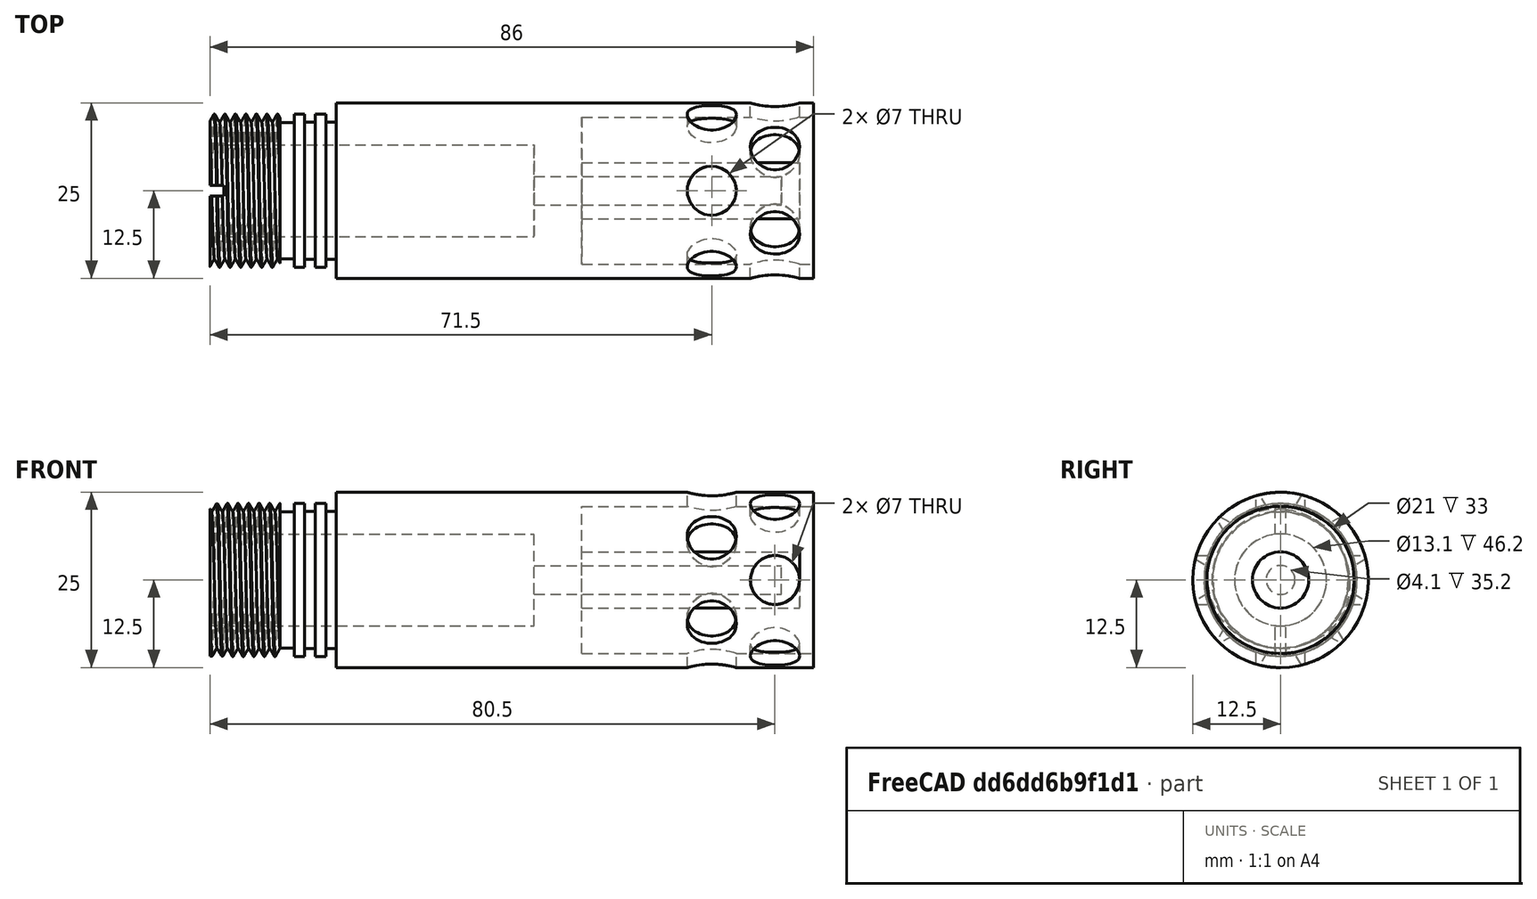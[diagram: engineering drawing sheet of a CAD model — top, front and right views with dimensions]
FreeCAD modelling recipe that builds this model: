
FCSTD DOCUMENT  (FreeCAD 0.17R13541 (Git))
Label: ERG-T-04-HEAD-01
License: All rights reserved
LicenseURL: http://en.wikipedia.org/wiki/All_rights_reserved
objects: Drawing::FeatureViewPython×37, Part::Cylinder×25, Part::Cut×13, Part::MultiFuse×9, Drawing::FeatureViewPart×4, Part::Helix×1, Sketcher::SketchObject×1, Part::Sweep×1, Part::Box×1, Drawing::FeaturePage×1
note: 51 computed .brp shape members not serialized (recipe doc carries the construction recipe); baked Part::Feature solids carry a one-line shape summary decoded from their .brp

FEATURE [Part::Cylinder] Cylinder072  label="Cylinder077"
  Angle = 360
  AttacherType = Attacher::AttachEngine3D
  Height = 18
  Placement = pos=(180.5,0,0) rot=(0,1,0;1.5708rad)
  Radius = 10.9
FEATURE [Part::Cylinder] Cylinder074  label="Cylinder083"
  Angle = 360
  AttacherType = Attacher::AttachEngine3D
  Height = 46.2
  Placement = pos=(180.5,0,0) rot=(0,1,0;1.5708rad)
  Radius = 6.55
FEATURE [Part::Cylinder] Cylinder075  label="Cylinder084"
  Angle = 360
  AttacherType = Attacher::AttachEngine3D
  Height = 53
  Placement = pos=(180.5,0,0) rot=(0,1,0;1.5708rad)
  Radius = 12.5
FEATURE [Part::Cylinder] Cylinder076  label="Cylinder085"
  Angle = 360
  AttacherType = Attacher::AttachEngine3D
  Height = 18
  Placement = pos=(180.5,0,0) rot=(0,1,0;1.5708rad)
  Radius = 12.5
FEATURE [Part::Cylinder] Cylinder077  label="Cylinder086"
  Angle = 360
  AttacherType = Attacher::AttachEngine3D
  Height = 31
  Placement = pos=(233.5,0,0) rot=(0,1,0;1.5708rad)
  Radius = 4
FEATURE [Part::Cut] Cut065
  Base = -> Cylinder076
  Tool = -> Cylinder072
FEATURE [Part::Cylinder] Cylinder080  label="Cylinder089"
  Angle = 360
  AttacherType = Attacher::AttachEngine3D
  Height = 35.2
  Placement = pos=(226.7,0,0) rot=(0,1,0;1.5708rad)
  Radius = 2.05
FEATURE [Part::MultiFuse] Fusion017  label="cavity"
  Shapes = -> [Cylinder080,Cylinder074]
FEATURE [Part::Helix] Helix019
  Angle = 0
  AttacherType = Attacher::AttachEngine3D
  Height = 17
  LocalCoord = 0
  Pitch = 1.5
  Placement = pos=(157,0,0) rot=(0,1,0;1.5708rad)
  Radius = 10.5
  Style = 1
FEATURE [Sketcher::SketchObject] Sketch023  label="T022"
  Placement = pos=(157,0,-11.01) rot=(1,0,0;1.5708rad)
  sketch-geometry (3):
    g0: LineSegment StartX=0 StartY=1.29904 StartZ=0 EndX=-0.75 EndY=0 EndZ=0
    g1: LineSegment StartX=0.75 StartY=0 StartZ=0 EndX=0 EndY=1.29904 EndZ=0
    g2: LineSegment StartX=-0.75 StartY=0 StartZ=0 EndX=0.75 EndY=0 EndZ=0
  constraints (9):
    c: PointOnObject(g1,g-1)
    c: Coincident(g1,g0)
    c: Coincident(g2,g0)
    c: Coincident(g2,g1)
    c: Horizontal(g2)
    c: Symmetric(g0,g1,g-2)
    c: Distance(g0,g1) = 1.5
    c: Angle(g1,g2) = 1.0472
    c: Angle(g2,g0) = 1.0472
FEATURE [Part::Sweep] Sweep016
  Frenet = true
  Sections = -> [Sketch023]
  Solid = true
  Spine = -> Helix019
  Transition = 1
FEATURE [Part::Cylinder] Cylinder084  label="Cylinder092"
  Angle = 360
  AttacherType = Attacher::AttachEngine3D
  Height = 1.5
  Placement = pos=(178,0,0) rot=(0,1,0;1.5708rad)
  Radius = 11
FEATURE [Part::Cylinder] Cylinder085  label="Cylinder093"
  Angle = 360
  AttacherType = Attacher::AttachEngine3D
  Height = 1.5
  Placement = pos=(178,0,0) rot=(0,1,0;1.5708rad)
  Radius = 9.8
FEATURE [Part::Cut] Cut071  label="circ2"
  Base = -> Cylinder084
  Placement = pos=(16,0,0) rot=(0,0,1;0rad)
  Tool = -> Cylinder085
FEATURE [Part::Cylinder] Cylinder086  label="Cylinder094"
  Angle = 360
  AttacherType = Attacher::AttachEngine3D
  Height = 2
  Placement = pos=(178,0,0) rot=(0,1,0;1.5708rad)
  Radius = 11
FEATURE [Part::Cylinder] Cylinder087  label="Cylinder095"
  Angle = 360
  AttacherType = Attacher::AttachEngine3D
  Height = 2
  Placement = pos=(178,0,0) rot=(0,1,0;1.5708rad)
  Radius = 9.7
FEATURE [Part::Cut] Cut072  label="circ1"
  Base = -> Cylinder086
  Placement = pos=(12.5,0,0) rot=(0,0,1;0rad)
  Tool = -> Cylinder087
FEATURE [Part::Cylinder] Cylinder088  label="Cylinder096"
  Angle = 360
  AttacherType = Attacher::AttachEngine3D
  Height = 10
  Placement = pos=(178,0,0) rot=(0,1,0;1.5708rad)
  Radius = 9
FEATURE [Part::Cylinder] Cylinder089  label="Cylinder097"
  Angle = 360
  AttacherType = Attacher::AttachEngine3D
  Height = 10
  Placement = pos=(178,0,0) rot=(0,1,0;1.5708rad)
  Radius = 11.5
FEATURE [Part::Cut] Cut074
  Base = -> Cylinder089
  Placement = pos=(-10.5,0,0) rot=(0,0,1;0rad)
  Tool = -> Cylinder088
FEATURE [Part::Box] Box  label="Cube"
  AttacherType = Attacher::AttachEngine3D
  Height = 30
  Length = 2
  Placement = pos=(180.5,-0.75,-15) rot=(0,0,1;0rad)
  Width = 1.5
FEATURE [Part::Cylinder] Cylinder091  label="Cylinder099"
  Angle = 360
  AttacherType = Attacher::AttachEngine3D
  Height = 35
  Placement = pos=(198.5,0,0) rot=(0,1,0;1.5708rad)
  Radius = 12.5
FEATURE [Part::Cylinder] Cylinder092  label="Cylinder100"
  Angle = 360
  AttacherType = Attacher::AttachEngine3D
  Height = 35
  Placement = pos=(198.5,0,0) rot=(0,1,0;1.5708rad)
  Radius = 10.9
FEATURE [Part::Cut] Cut
  Base = -> Cylinder091
  Tool = -> Cylinder092
FEATURE [Part::Cylinder] Cylinder093  label="Cylinder101"
  Angle = 360
  AttacherType = Attacher::AttachEngine3D
  Height = 1.5
  Placement = pos=(178,0,0) rot=(0,1,0;1.5708rad)
  Radius = 11
FEATURE [Part::Cylinder] Cylinder094  label="Cylinder102"
  Angle = 360
  AttacherType = Attacher::AttachEngine3D
  Height = 1.5
  Placement = pos=(178,0,0) rot=(0,1,0;1.5708rad)
  Radius = 9.8
FEATURE [Part::Cut] Cut076  label="circ3"
  Base = -> Cylinder093
  Placement = pos=(19,0,0) rot=(0,0,1;0rad)
  Tool = -> Cylinder094
FEATURE [Part::MultiFuse] Fusion019
  Shapes = -> [Cut,Cut065]
FEATURE [Part::MultiFuse] Fusion020
  Shapes = -> [Cylinder075,Cylinder077]
FEATURE [Part::Cut] Cut077  label="body"
  Base = -> Fusion020
  Tool = -> Fusion019
FEATURE [Part::Cut] Cut078  label="thread"
  Base = -> Sweep016
  Placement = pos=(23,0,0) rot=(0,0,1;0rad)
  Tool = -> Cut074
FEATURE [Part::MultiFuse] Fusion021  label="cutstuff"
  Shapes = -> [Cut078,Cut076,Cut072,Cut071]
FEATURE [Part::Cut] Cut079  label="outside"
  Base = -> Cut077
  Tool = -> Fusion021
FEATURE [Part::Cut] Cut080  label="holder01"
  Base = -> Cut079
  Tool = -> Fusion017
FEATURE [Part::Cut] Cut081  label="HOLDER"
  Base = -> Cut080
  Tool = -> Box
FEATURE [Part::Cylinder] Cylinder079  label="Cylinder088"
  Angle = 360
  AttacherType = Attacher::AttachEngine3D
  Height = 50
  Placement = pos=(214.2,21.6506,12.5) rot=(1,0,0;2.0944rad)
  Radius = 3.5
FEATURE [Part::Cylinder] Cylinder081  label="Cylinder090"
  Angle = 360
  AttacherType = Attacher::AttachEngine3D
  Height = 50
  Placement = pos=(214.2,0,-25) rot=(0,1,0;0rad)
  Radius = 3.5
FEATURE [Part::Cylinder] Cylinder082  label="Cylinder078"
  Angle = 360
  AttacherType = Attacher::AttachEngine3D
  Height = 50
  Placement = pos=(214.2,0,-25) rot=(0,1,0;0rad)
  Radius = 3.5
FEATURE [Part::Cylinder] Cylinder090  label="Cylinder098"
  Angle = 360
  AttacherType = Attacher::AttachEngine3D
  Height = 68
  Placement = pos=(198.2,0,0) rot=(0,1,0;1.5708rad)
  Radius = 12.5
FEATURE [Part::Cylinder] Cylinder071  label="Cylinder081"
  Angle = 360
  AttacherType = Attacher::AttachEngine3D
  Height = 33
  Placement = pos=(233.2,0,0) rot=(0,1,0;1.5708rad)
  Radius = 10.5
FEATURE [Part::Cylinder] Cylinder095  label="Cylinder103"
  Angle = 360
  AttacherType = Attacher::AttachEngine3D
  Height = 35
  Placement = pos=(198.2,0,0) rot=(0,1,0;1.5708rad)
  Radius = 10.9
FEATURE [Part::MultiFuse] Fusion022  label="cavity001"
  Shapes = -> [Cylinder095,Cylinder071]
FEATURE [Part::Cut] Cut082  label="body001"
  Base = -> Cylinder090
  Tool = -> Fusion022
FEATURE [Part::Cylinder] Cylinder070  label="Cylinder075"
  Angle = 360
  AttacherType = Attacher::AttachEngine3D
  Height = 50
  Placement = pos=(214.2,-21.6506,12.5) rot=(-1,0,0;2.0944rad)
  Radius = 3.5
FEATURE [Part::Cylinder] Cylinder078  label="Cylinder087"
  Angle = 360
  AttacherType = Attacher::AttachEngine3D
  Height = 50
  Placement = pos=(214.2,21.6506,12.5) rot=(1,0,0;2.0944rad)
  Radius = 3.5
FEATURE [Part::MultiFuse] Fusion016
  Placement = pos=(37.5,0,0) rot=(1,0,0;0rad)
  Shapes = -> [Cylinder081,Cylinder070,Cylinder078]
FEATURE [Part::Cylinder] Cylinder073  label="Cylinder082"
  Angle = 360
  AttacherType = Attacher::AttachEngine3D
  Height = 50
  Placement = pos=(214.2,-21.6506,12.5) rot=(-1,0,0;2.0944rad)
  Radius = 3.5
FEATURE [Part::MultiFuse] Fusion018
  Placement = pos=(46.5,0,0) rot=(1,0,0;0.523599rad)
  Shapes = -> [Cylinder082,Cylinder073,Cylinder079]
FEATURE [Part::MultiFuse] Fusion  label="holesticks"
  Shapes = -> [Fusion016,Fusion018]
FEATURE [Part::Cut] Cut001  label="CAP"
  Base = -> Cut082
  Placement = pos=(0.3,0,0) rot=(0,0,1;0rad)
  Tool = -> Fusion
FEATURE [Part::MultiFuse] Fusion023  label="SensorHead"
  Shapes = -> [Cut081,Cut001]
FEATURE [Drawing::FeatureViewPart] Ortho  label="Ortho_0_0"
  Direction = (0,0,1)
  HiddenWidth = 0.15
  LineWidth = 0.35
  Rotation = 0
  Scale = 1.5
  ShowHiddenLines = true
  ShowSmoothLines = false
  Source = -> Fusion023
  Tolerance = 0.05
  ViewResult = <blob: 68235 chars omitted>
  Visible = true
  X = -186.75
  Y = 110.035
FEATURE [Drawing::FeatureViewPart] Ortho001  label="Ortho_0_1"
  Direction = (0,1,0)
  HiddenWidth = 0.15
  LineWidth = 0.35
  Rotation = 90
  Scale = 1.5
  ShowHiddenLines = true
  ShowSmoothLines = false
  Source = -> Fusion023
  Tolerance = 0.05
  ViewResult = <blob: 71833 chars omitted>
  Visible = true
  X = -186.75
  Y = 48.0517
FEATURE [Drawing::FeatureViewPart] Ortho002  label="Ortho_-1_0"
  Direction = (-1,0,0)
  HiddenWidth = 0.15
  LineWidth = 0.35
  Rotation = 180
  Scale = 1.5
  ShowHiddenLines = false
  ShowSmoothLines = false
  Source = -> Fusion023
  Tolerance = 0.05
  ViewResult = <blob: 14016 chars omitted>
  Visible = true
  X = 53.8386
  Y = 110.035
FEATURE [Drawing::FeatureViewPart] Ortho003  label="Ortho_1_0"
  Direction = (1,0,0)
  HiddenWidth = 0.15
  LineWidth = 0.35
  Rotation = 180
  Scale = 1.5
  ShowHiddenLines = false
  ShowSmoothLines = false
  Source = -> Fusion023
  Tolerance = 0.05
  ViewResult = <blob: 12692 chars omitted>
  Visible = true
  X = 243.161
  Y = 110.035
FEATURE [Drawing::FeatureViewPython] dia001  # drawing view (typed FeaturePython)
  Rotation = 0
  ViewResult = <g>  <circle cx ="243.161000" cy ="110.035000" r="0.250000" stroke="none" fill="rgb(255,0,0)" /> \n<line x1="265.734526" y1="88.241056" x2="238.844478" y2="114.202450" style="stroke:rgb(255,0,0);stroke-width:0.10" />\n<polygon points="247.477522,105.867550 245.691394,106.896990 245.678971,107.603988 246.385969,107.616410" style="fill:rgb(255,0,0);stroke:rgb(255,0,0);stroke-width:0" />\n<polygon points="238.844478,114.202450 240.630606,113.173010 240.643029,112.466012 239.936031,112.453590" style="fill:rgb(255,0,0);stroke:rgb(255,0,0);stroke-width:0" />\n<line x1="265.734526" y1="88.241056" x2="277.870832" y2="88.241056" style="stroke:rgb(255,0,0);stroke-width:0.10" />\n<text x="271.802679" y="86.241056" font-family="inherit" font-size="3.6" fill="rgb(0,0,0)" text-anchor="middle" transform="rotate(0.000000 271.802679,86.241056)" >Ø8</text> </g>
  Visible = true
  X = 0
  Y = 0
  arrowL1 = 2
  arrowL2 = 0.5
  arrowW = 1
  arrow_scheme = 0
  autoPlaceOffset = 2
  autoPlaceText = true
  centerPointDia = 0.5
  click1_x = 265.735
  click1_y = 88.2411
  click2_x = 277.871
  click2_y = 88.4939
  click3_x = 277.871
  click3_y = 88.4939
  comma_decimal_place = false
  lineColor = rgb(255,0,0)
  strokeWidth = 0.1
  textFormat_circular = Ø%(value)3.3f
  textRenderer_color = rgb(0,0,0)
  textRenderer_family = inherit
  textRenderer_size = 3.6
  unit_custom_scale = 1
  unit_scheme = 0
FEATURE [Drawing::FeatureViewPython] dia002  # drawing view (typed FeaturePython)
  Rotation = 0
  ViewResult = <g>  <circle cx ="243.161000" cy ="110.035000" r="0.250000" stroke="none" fill="rgb(255,0,0)" /> \n<line x1="263.711809" y1="131.476645" x2="232.262781" y2="98.664366" style="stroke:rgb(255,0,0);stroke-width:0.10" />\n<polygon points="254.059219,121.405634 253.036290,119.615769 252.329343,119.600772 252.314345,120.307720" style="fill:rgb(255,0,0);stroke:rgb(255,0,0);stroke-width:0" />\n<polygon points="232.262781,98.664366 233.285710,100.454231 233.992657,100.469228 234.007655,99.762280" style="fill:rgb(255,0,0);stroke:rgb(255,0,0);stroke-width:0" />\n<line x1="263.711809" y1="131.476645" x2="273.319717" y2="131.476645" style="stroke:rgb(255,0,0);stroke-width:0.10" />\n<text x="268.515763" y="129.476645" font-family="inherit" font-size="3.6" fill="rgb(0,0,0)" text-anchor="middle" transform="rotate(0.000000 268.515763,129.476645)" >Ø21</text> </g>
  Visible = true
  X = 0
  Y = 0
  arrowL1 = 2
  arrowL2 = 0.5
  arrowW = 1
  arrow_scheme = 0
  autoPlaceOffset = 2
  autoPlaceText = true
  centerPointDia = 0.5
  click1_x = 263.712
  click1_y = 131.477
  click2_x = 273.32
  click2_y = 132.994
  click3_x = 273.32
  click3_y = 132.994
  comma_decimal_place = false
  lineColor = rgb(255,0,0)
  strokeWidth = 0.1
  textFormat_circular = Ø%(value)3.3f
  textRenderer_color = rgb(0,0,0)
  textRenderer_family = inherit
  textRenderer_size = 3.6
  unit_custom_scale = 1
  unit_scheme = 0
FEATURE [Drawing::FeatureViewPython] dia003  # drawing view (typed FeaturePython)
  Rotation = 0
  ViewResult = <g>  <circle cx ="243.161000" cy ="110.035000" r="0.250000" stroke="none" fill="rgb(255,0,0)" /> \n<line x1="255.115259" y1="139.820355" x2="236.177225" y2="92.634155" style="stroke:rgb(255,0,0);stroke-width:0.10" />\n<polygon points="250.144775,127.435845 249.863861,125.393521 249.213605,125.115732 248.935816,125.765989" style="fill:rgb(255,0,0);stroke:rgb(255,0,0);stroke-width:0" />\n<polygon points="236.177225,92.634155 236.458139,94.676479 237.108395,94.954268 237.386184,94.304011" style="fill:rgb(255,0,0);stroke:rgb(255,0,0);stroke-width:0" />\n<line x1="255.115259" y1="139.820355" x2="263.458969" y2="139.820355" style="stroke:rgb(255,0,0);stroke-width:0.10" />\n<text x="259.287114" y="137.820355" font-family="inherit" font-size="3.6" fill="rgb(0,0,0)" text-anchor="middle" transform="rotate(0.000000 259.287114,137.820355)" >Ø25</text> </g>
  Visible = true
  X = 0
  Y = 0
  arrowL1 = 2
  arrowL2 = 0.5
  arrowW = 1
  arrow_scheme = 0
  autoPlaceOffset = 2
  autoPlaceText = true
  centerPointDia = 0.5
  click1_x = 255.115
  click1_y = 139.82
  click2_x = 263.459
  click2_y = 143.36
  click3_x = 263.459
  click3_y = 143.36
  comma_decimal_place = false
  lineColor = rgb(255,0,0)
  strokeWidth = 0.1
  textFormat_circular = Ø%(value)3.3f
  textRenderer_color = rgb(0,0,0)
  textRenderer_family = inherit
  textRenderer_size = 3.6
  unit_custom_scale = 1
  unit_scheme = 0
FEATURE [Drawing::FeatureViewPython] dia004  # drawing view (typed FeaturePython)
  Rotation = 0
  ViewResult = <g>  <circle cx ="53.838600" cy ="110.035008" r="0.250000" stroke="none" fill="rgb(255,0,0)" /> \n<line x1="21.744214" y1="149.681103" x2="60.020464" y2="102.398570" style="stroke:rgb(255,0,0);stroke-width:0.10" />\n<polygon points="47.656736,117.671446 49.303753,116.431553 49.229729,115.728332 48.526508,115.802356" style="fill:rgb(255,0,0);stroke:rgb(255,0,0);stroke-width:0" />\n<polygon points="60.020464,102.398570 58.373447,103.638463 58.447471,104.341684 59.150692,104.267660" style="fill:rgb(255,0,0);stroke:rgb(255,0,0);stroke-width:0" />\n<line x1="21.744214" y1="149.681103" x2="12.389145" y2="149.681103" style="stroke:rgb(255,0,0);stroke-width:0.10" />\n<text x="17.066680" y="147.681103" font-family="inherit" font-size="3.6" fill="rgb(0,0,0)" text-anchor="middle" transform="rotate(0.000000 17.066680,147.681103)" >Ø13.1</text> </g>
  Visible = true
  X = 0
  Y = 0
  arrowL1 = 2
  arrowL2 = 0.5
  arrowW = 1
  arrow_scheme = 0
  autoPlaceOffset = 2
  autoPlaceText = true
  centerPointDia = 0.5
  click1_x = 21.7442
  click1_y = 149.681
  click2_x = 12.3891
  click2_y = 148.67
  click3_x = 12.3891
  click3_y = 148.67
  comma_decimal_place = false
  lineColor = rgb(255,0,0)
  strokeWidth = 0.1
  textFormat_circular = Ø%(value)3.3f
  textRenderer_color = rgb(0,0,0)
  textRenderer_family = inherit
  textRenderer_size = 3.6
  unit_custom_scale = 1
  unit_scheme = 0
FEATURE [Drawing::FeatureViewPython] dia005  # drawing view (typed FeaturePython)
  Rotation = 0
  ViewResult = <g>  <circle cx ="53.838600" cy ="110.035000" r="0.250000" stroke="none" fill="rgb(255,0,0)" /> \n<line x1="31.099283" y1="81.667224" x2="55.761862" y2="112.434310" style="stroke:rgb(255,0,0);stroke-width:0.10" />\n<polygon points="51.915338,107.635690 52.776108,109.508942 53.478966,109.586349 53.556372,108.883491" style="fill:rgb(255,0,0);stroke:rgb(255,0,0);stroke-width:0" />\n<polygon points="55.761862,112.434310 54.901092,110.561058 54.198234,110.483651 54.120828,111.186509" style="fill:rgb(255,0,0);stroke:rgb(255,0,0);stroke-width:0" />\n<line x1="31.099283" y1="81.667224" x2="20.480016" y2="81.667224" style="stroke:rgb(255,0,0);stroke-width:0.10" />\n<text x="25.789650" y="79.667224" font-family="inherit" font-size="3.6" fill="rgb(0,0,0)" text-anchor="middle" transform="rotate(0.000000 25.789650,79.667224)" >Ø4.1</text> </g>
  Visible = true
  X = 0
  Y = 0
  arrowL1 = 2
  arrowL2 = 0.5
  arrowW = 1
  arrow_scheme = 0
  autoPlaceOffset = 2
  autoPlaceText = true
  centerPointDia = 0.5
  click1_x = 31.0993
  click1_y = 81.6672
  click2_x = 20.48
  click2_y = 80.403
  click3_x = 20.48
  click3_y = 80.403
  comma_decimal_place = false
  lineColor = rgb(255,0,0)
  strokeWidth = 0.1
  textFormat_circular = Ø%(value)3.3f
  textRenderer_color = rgb(0,0,0)
  textRenderer_family = inherit
  textRenderer_size = 3.6
  unit_custom_scale = 1
  unit_scheme = 0
FEATURE [Drawing::FeatureViewPython] dia006  # drawing view (typed FeaturePython)
  Rotation = 0
  ViewResult = <g>  <circle cx ="53.838600" cy ="110.035000" r="0.250000" stroke="none" fill="rgb(255,0,0)" /> \n<line x1="31.857802" y1="162.323088" x2="61.104773" y2="92.750173" style="stroke:rgb(255,0,0);stroke-width:0.10" />\n<polygon points="46.572427,127.319827 47.808414,125.669876 47.541250,125.015183 46.886557,125.282347" style="fill:rgb(255,0,0);stroke:rgb(255,0,0);stroke-width:0" />\n<polygon points="61.104773,92.750173 59.868786,94.400124 60.135950,95.054817 60.790643,94.787653" style="fill:rgb(255,0,0);stroke:rgb(255,0,0);stroke-width:0" />\n<line x1="31.857802" y1="162.323088" x2="18.710138" y2="162.323088" style="stroke:rgb(255,0,0);stroke-width:0.10" />\n<text x="25.283970" y="160.323088" font-family="inherit" font-size="3.6" fill="rgb(0,0,0)" text-anchor="middle" transform="rotate(0.000000 25.283970,160.323088)" >Ø25</text> </g>
  Visible = true
  X = 0
  Y = 0
  arrowL1 = 2
  arrowL2 = 0.5
  arrowW = 1
  arrow_scheme = 0
  autoPlaceOffset = 2
  autoPlaceText = true
  centerPointDia = 0.5
  click1_x = 31.8578
  click1_y = 162.323
  click2_x = 18.7101
  click2_y = 165.104
  click3_x = 18.7101
  click3_y = 165.104
  comma_decimal_place = false
  lineColor = rgb(255,0,0)
  strokeWidth = 0.1
  textFormat_circular = Ø%(value)3.3f
  textRenderer_color = rgb(0,0,0)
  textRenderer_family = inherit
  textRenderer_size = 3.6
  unit_custom_scale = 1
  unit_scheme = 0
FEATURE [Drawing::FeatureViewPython] dim001  # drawing view (typed FeaturePython)
  Rotation = 0
  ViewResult = <g> \n  <line x1="84.000000" y1="31.740400" x2="84.000000" y2="16.093481" style="stroke:rgb(255,0,0);stroke-width:0.10" />\n<line x1="213.000000" y1="29.301700" x2="213.000000" y2="16.093481" style="stroke:rgb(255,0,0);stroke-width:0.10" />\n<line x1="84.000000" y1="17.093481" x2="213.000000" y2="17.093481" style="stroke:rgb(255,0,0);stroke-width:0.10" /> \n  <polygon points="213.000000,17.093481 211.000000,16.593481 210.500000,17.093481 211.000000,17.593481" style="fill:rgb(255,0,0);stroke:rgb(255,0,0);stroke-width:0" /><polygon points="84.000000,17.093481 86.000000,17.593481 86.500000,17.093481 86.000000,16.593481" style="fill:rgb(255,0,0);stroke:rgb(255,0,0);stroke-width:0" /> \n  <text x="148.500000" y="15.093481" font-family="inherit" font-size="3.6" fill="rgb(0,0,0)" text-anchor="middle" transform="rotate(0.000000 148.500000,15.093481)" >86</text> </g>
  Visible = true
  X = 0
  Y = 0
  arrowL1 = 2
  arrowL2 = 0.5
  arrowW = 1
  arrow_scheme = 0
  autoPlaceOffset = 2
  autoPlaceText = true
  click1_x = 212.851
  click1_y = 17.0935
  click2_x = 212.851
  click2_y = 17.0935
  comma_decimal_place = false
  dimension_line_overshoot = 1
  gap_datum_points = 0
  halfDimension_linear = false
  lineColor = rgb(255,0,0)
  strokeWidth = 0.1
  textFormat_linear = %(value)3.3f
  textRenderer_color = rgb(0,0,0)
  textRenderer_family = inherit
  textRenderer_size = 3.6
  unit_custom_scale = 1
  unit_scheme = 0
FEATURE [Drawing::FeatureViewPython] dim002  # drawing view (typed FeaturePython)
  Rotation = 0
  ViewResult = <g> \n  <line x1="111.000000" y1="29.301700" x2="111.000000" y2="22.818722" style="stroke:rgb(255,0,0);stroke-width:0.10" />\n<line x1="213.000000" y1="29.301700" x2="213.000000" y2="22.818722" style="stroke:rgb(255,0,0);stroke-width:0.10" />\n<line x1="111.000000" y1="23.818722" x2="213.000000" y2="23.818722" style="stroke:rgb(255,0,0);stroke-width:0.10" /> \n  <polygon points="213.000000,23.818722 211.000000,23.318722 210.500000,23.818722 211.000000,24.318722" style="fill:rgb(255,0,0);stroke:rgb(255,0,0);stroke-width:0" /><polygon points="111.000000,23.818722 113.000000,24.318722 113.500000,23.818722 113.000000,23.318722" style="fill:rgb(255,0,0);stroke:rgb(255,0,0);stroke-width:0" /> \n  <text x="162.000000" y="21.818722" font-family="inherit" font-size="3.6" fill="rgb(0,0,0)" text-anchor="middle" transform="rotate(0.000000 162.000000,21.818722)" >68</text> </g>
  Visible = true
  X = 0
  Y = 0
  arrowL1 = 2
  arrowL2 = 0.5
  arrowW = 1
  arrow_scheme = 0
  autoPlaceOffset = 2
  autoPlaceText = true
  click1_x = 212.34
  click1_y = 23.8187
  click2_x = 212.34
  click2_y = 23.8187
  comma_decimal_place = false
  dimension_line_overshoot = 1
  gap_datum_points = 0
  halfDimension_linear = false
  lineColor = rgb(255,0,0)
  strokeWidth = 0.1
  textFormat_linear = %(value)3.3f
  textRenderer_color = rgb(0,0,0)
  textRenderer_family = inherit
  textRenderer_size = 3.6
  unit_custom_scale = 1
  unit_scheme = 0
FEATURE [Drawing::FeatureViewPython] dim003  # drawing view (typed FeaturePython)
  Rotation = 0
  ViewResult = <g> \n  <line x1="111.000000" y1="29.301700" x2="111.000000" y2="22.825336" style="stroke:rgb(255,0,0);stroke-width:0.10" />\n<line x1="84.000000" y1="31.740400" x2="84.000000" y2="22.825336" style="stroke:rgb(255,0,0);stroke-width:0.10" />\n<line x1="111.000000" y1="23.825336" x2="84.000000" y2="23.825336" style="stroke:rgb(255,0,0);stroke-width:0.10" /> \n  <polygon points="84.000000,23.825336 86.000000,24.325336 86.500000,23.825336 86.000000,23.325336" style="fill:rgb(255,0,0);stroke:rgb(255,0,0);stroke-width:0" /><polygon points="111.000000,23.825336 109.000000,23.325336 108.500000,23.825336 109.000000,24.325336" style="fill:rgb(255,0,0);stroke:rgb(255,0,0);stroke-width:0" /> \n  <text x="97.500000" y="21.825336" font-family="inherit" font-size="3.6" fill="rgb(0,0,0)" text-anchor="middle" transform="rotate(0.000000 97.500000,21.825336)" >18</text> </g>
  Visible = true
  X = 0
  Y = 0
  arrowL1 = 2
  arrowL2 = 0.5
  arrowW = 1
  arrow_scheme = 0
  autoPlaceOffset = 2
  autoPlaceText = true
  click1_x = 91.4514
  click1_y = 23.8253
  click2_x = 91.4514
  click2_y = 23.8253
  comma_decimal_place = false
  dimension_line_overshoot = 1
  gap_datum_points = 0
  halfDimension_linear = false
  lineColor = rgb(255,0,0)
  strokeWidth = 0.1
  textFormat_linear = %(value)3.3f
  textRenderer_color = rgb(0,0,0)
  textRenderer_family = inherit
  textRenderer_size = 3.6
  unit_custom_scale = 1
  unit_scheme = 0
FEATURE [Drawing::FeatureViewPython] dim004  # drawing view (typed FeaturePython)
  Rotation = 0
  ViewResult = <g> \n  <line x1="99.000000" y1="33.472075" x2="99.000000" y2="27.704008" style="stroke:rgb(255,0,0);stroke-width:0.10" />\n<line x1="111.000000" y1="29.301700" x2="111.000000" y2="27.704008" style="stroke:rgb(255,0,0);stroke-width:0.10" />\n<line x1="99.000000" y1="28.704008" x2="111.000000" y2="28.704008" style="stroke:rgb(255,0,0);stroke-width:0.10" /> \n  <polygon points="111.000000,28.704008 109.000000,28.204008 108.500000,28.704008 109.000000,29.204008" style="fill:rgb(255,0,0);stroke:rgb(255,0,0);stroke-width:0" /><polygon points="99.000000,28.704008 101.000000,29.204008 101.500000,28.704008 101.000000,28.204008" style="fill:rgb(255,0,0);stroke:rgb(255,0,0);stroke-width:0" /> \n  <text x="105.000000" y="26.704008" font-family="inherit" font-size="3.6" fill="rgb(0,0,0)" text-anchor="middle" transform="rotate(0.000000 105.000000,26.704008)" >8</text> </g>
  Visible = true
  X = 0
  Y = 0
  arrowL1 = 2
  arrowL2 = 0.5
  arrowW = 1
  arrow_scheme = 0
  autoPlaceOffset = 2
  autoPlaceText = true
  click1_x = 110.878
  click1_y = 28.704
  click2_x = 110.878
  click2_y = 28.704
  comma_decimal_place = false
  dimension_line_overshoot = 1
  gap_datum_points = 0
  halfDimension_linear = false
  lineColor = rgb(255,0,0)
  strokeWidth = 0.1
  textFormat_linear = %(value)3.3f
  textRenderer_color = rgb(0,0,0)
  textRenderer_family = inherit
  textRenderer_size = 3.6
  unit_custom_scale = 1
  unit_scheme = 0
FEATURE [Drawing::FeatureViewPython] dim005  # drawing view (typed FeaturePython)
  Rotation = 0
  ViewResult = <g> \n  <line x1="99.000000" y1="33.472075" x2="99.000000" y2="27.704008" style="stroke:rgb(255,0,0);stroke-width:0.10" />\n<line x1="84.000000" y1="31.740400" x2="84.000000" y2="27.704008" style="stroke:rgb(255,0,0);stroke-width:0.10" />\n<line x1="99.000000" y1="28.704008" x2="84.000000" y2="28.704008" style="stroke:rgb(255,0,0);stroke-width:0.10" /> \n  <polygon points="84.000000,28.704008 86.000000,29.204008 86.500000,28.704008 86.000000,28.204008" style="fill:rgb(255,0,0);stroke:rgb(255,0,0);stroke-width:0" /><polygon points="99.000000,28.704008 97.000000,28.204008 96.500000,28.704008 97.000000,29.204008" style="fill:rgb(255,0,0);stroke:rgb(255,0,0);stroke-width:0" /> \n  <text x="91.500000" y="26.704008" font-family="inherit" font-size="3.6" fill="rgb(0,0,0)" text-anchor="middle" transform="rotate(0.000000 91.500000,26.704008)" >10</text> </g>
  Visible = true
  X = 0
  Y = 0
  arrowL1 = 2
  arrowL2 = 0.5
  arrowW = 1
  arrow_scheme = 0
  autoPlaceOffset = 2
  autoPlaceText = true
  click1_x = 84.2565
  click1_y = 28.704
  click2_x = 84.2565
  click2_y = 28.704
  comma_decimal_place = false
  dimension_line_overshoot = 1
  gap_datum_points = 0
  halfDimension_linear = false
  lineColor = rgb(255,0,0)
  strokeWidth = 0.1
  textFormat_linear = %(value)3.3f
  textRenderer_color = rgb(0,0,0)
  textRenderer_family = inherit
  textRenderer_size = 3.6
  unit_custom_scale = 1
  unit_scheme = 0
FEATURE [Drawing::FeatureViewPython] dim006  # drawing view (typed FeaturePython)
  Rotation = 0
  ViewResult = <g> \n  <line x1="84.000000" y1="63.271900" x2="84.000000" y2="77.638701" style="stroke:rgb(255,0,0);stroke-width:0.10" />\n<line x1="153.300000" y1="57.876700" x2="153.300000" y2="77.638701" style="stroke:rgb(255,0,0);stroke-width:0.10" />\n<line x1="84.000000" y1="76.638701" x2="153.300000" y2="76.638701" style="stroke:rgb(255,0,0);stroke-width:0.10" /> \n  <polygon points="153.300000,76.638701 151.300000,76.138701 150.800000,76.638701 151.300000,77.138701" style="fill:rgb(255,0,0);stroke:rgb(255,0,0);stroke-width:0" /><polygon points="84.000000,76.638701 86.000000,77.138701 86.500000,76.638701 86.000000,76.138701" style="fill:rgb(255,0,0);stroke:rgb(255,0,0);stroke-width:0" /> \n  <text x="118.650000" y="74.638701" font-family="inherit" font-size="3.6" fill="rgb(0,0,0)" text-anchor="middle" transform="rotate(0.000000 118.650000,74.638701)" >46.2</text> </g>
  Visible = true
  X = 0
  Y = 0
  arrowL1 = 2
  arrowL2 = 0.5
  arrowW = 1
  arrow_scheme = 0
  autoPlaceOffset = 2
  autoPlaceText = true
  click1_x = 150.136
  click1_y = 76.6387
  click2_x = 150.136
  click2_y = 76.6387
  comma_decimal_place = false
  dimension_line_overshoot = 1
  gap_datum_points = 0
  halfDimension_linear = false
  lineColor = rgb(255,0,0)
  strokeWidth = 0.1
  textFormat_linear = %(value)3.3f
  textRenderer_color = rgb(0,0,0)
  textRenderer_family = inherit
  textRenderer_size = 3.6
  unit_custom_scale = 1
  unit_scheme = 0
FEATURE [Drawing::FeatureViewPython] dim007  # drawing view (typed FeaturePython)
  Rotation = 0
  ViewResult = <g> \n  <line x1="153.300000" y1="57.876700" x2="153.300000" y2="77.672934" style="stroke:rgb(255,0,0);stroke-width:0.10" />\n<line x1="206.100000" y1="51.126700" x2="206.100000" y2="77.672934" style="stroke:rgb(255,0,0);stroke-width:0.10" />\n<line x1="153.300000" y1="76.672934" x2="206.100000" y2="76.672934" style="stroke:rgb(255,0,0);stroke-width:0.10" /> \n  <polygon points="206.100000,76.672934 204.100000,76.172934 203.600000,76.672934 204.100000,77.172934" style="fill:rgb(255,0,0);stroke:rgb(255,0,0);stroke-width:0" /><polygon points="153.300000,76.672934 155.300000,77.172934 155.800000,76.672934 155.300000,76.172934" style="fill:rgb(255,0,0);stroke:rgb(255,0,0);stroke-width:0" /> \n  <text x="179.700000" y="74.672934" font-family="inherit" font-size="3.6" fill="rgb(0,0,0)" text-anchor="middle" transform="rotate(0.000000 179.700000,74.672934)" >35.2</text> </g>
  Visible = true
  X = 0
  Y = 0
  arrowL1 = 2
  arrowL2 = 0.5
  arrowW = 1
  arrow_scheme = 0
  autoPlaceOffset = 2
  autoPlaceText = true
  click1_x = 201.901
  click1_y = 76.6729
  click2_x = 201.901
  click2_y = 76.6729
  comma_decimal_place = false
  dimension_line_overshoot = 1
  gap_datum_points = 0
  halfDimension_linear = false
  lineColor = rgb(255,0,0)
  strokeWidth = 0.1
  textFormat_linear = %(value)3.3f
  textRenderer_color = rgb(0,0,0)
  textRenderer_family = inherit
  textRenderer_size = 3.6
  unit_custom_scale = 1
  unit_scheme = 0
FEATURE [Drawing::FeatureViewPython] dim008  # drawing view (typed FeaturePython)
  Rotation = 0
  ViewResult = <g> \n  <line x1="87.000000" y1="63.280300" x2="87.000000" y2="73.190913" style="stroke:rgb(255,0,0);stroke-width:0.10" />\n<line x1="84.000000" y1="63.271900" x2="84.000000" y2="73.190913" style="stroke:rgb(255,0,0);stroke-width:0.10" />\n<line x1="87.000000" y1="72.190913" x2="84.000000" y2="72.190913" style="stroke:rgb(255,0,0);stroke-width:0.10" /> \n  <polygon points="84.000000,72.190913 82.000000,71.690913 81.500000,72.190913 82.000000,72.690913" style="fill:rgb(255,0,0);stroke:rgb(255,0,0);stroke-width:0" /><polygon points="87.000000,72.190913 89.000000,72.690913 89.500000,72.190913 89.000000,71.690913" style="fill:rgb(255,0,0);stroke:rgb(255,0,0);stroke-width:0" /> \n  <text x="85.500000" y="70.190913" font-family="inherit" font-size="3.6" fill="rgb(0,0,0)" text-anchor="middle" transform="rotate(0.000000 85.500000,70.190913)" >2</text> </g>
  Visible = true
  X = 0
  Y = 0
  arrowL1 = 2
  arrowL2 = 0.5
  arrowW = 1
  arrow_scheme = 0
  autoPlaceOffset = 2
  autoPlaceText = true
  click1_x = 84.434
  click1_y = 72.1909
  click2_x = 84.434
  click2_y = 72.1909
  comma_decimal_place = false
  dimension_line_overshoot = 1
  gap_datum_points = 0
  halfDimension_linear = false
  lineColor = rgb(255,0,0)
  strokeWidth = 0.1
  textFormat_linear = %(value)3.3f
  textRenderer_color = rgb(0,0,0)
  textRenderer_family = inherit
  textRenderer_size = 3.6
  unit_custom_scale = 1
  unit_scheme = 0
FEATURE [Drawing::FeatureViewPython] dim011  # drawing view (typed FeaturePython)
  Rotation = 0
  ViewResult = <g> \n  <line x1="153.300000" y1="38.226700" x2="143.411508" y2="38.226700" style="stroke:rgb(255,0,0);stroke-width:0.10" />\n<line x1="153.300000" y1="57.876700" x2="143.411508" y2="57.876700" style="stroke:rgb(255,0,0);stroke-width:0.10" />\n<line x1="144.411508" y1="38.226700" x2="144.411508" y2="57.876700" style="stroke:rgb(255,0,0);stroke-width:0.10" /> \n  <polygon points="144.411508,57.876700 144.911508,55.876700 144.411508,55.376700 143.911508,55.876700" style="fill:rgb(255,0,0);stroke:rgb(255,0,0);stroke-width:0" /><polygon points="144.411508,38.226700 143.911508,40.226700 144.411508,40.726700 144.911508,40.226700" style="fill:rgb(255,0,0);stroke:rgb(255,0,0);stroke-width:0" /> \n  <text x="142.411508" y="48.051700" font-family="inherit" font-size="3.6" fill="rgb(0,0,0)" text-anchor="middle" transform="rotate(-90.000000 142.411508,48.051700)" >13.1</text> </g>
  Visible = true
  X = 0
  Y = 0
  arrowL1 = 2
  arrowL2 = 0.5
  arrowW = 1
  arrow_scheme = 0
  autoPlaceOffset = 2
  autoPlaceText = true
  click1_x = 144.412
  click1_y = 57.2204
  click2_x = 144.412
  click2_y = 57.2204
  comma_decimal_place = false
  dimension_line_overshoot = 1
  gap_datum_points = 0
  halfDimension_linear = false
  lineColor = rgb(255,0,0)
  strokeWidth = 0.1
  textFormat_linear = %(value)3.3f
  textRenderer_color = rgb(0,0,0)
  textRenderer_family = inherit
  textRenderer_size = 3.6
  unit_custom_scale = 1
  unit_scheme = 0
FEATURE [Drawing::FeatureViewPython] dim012  # drawing view (typed FeaturePython)
  Rotation = 0
  ViewResult = <g> \n  <line x1="153.300000" y1="44.976700" x2="161.873897" y2="44.976700" style="stroke:rgb(255,0,0);stroke-width:0.10" />\n<line x1="153.300000" y1="51.126700" x2="161.873897" y2="51.126700" style="stroke:rgb(255,0,0);stroke-width:0.10" />\n<line x1="160.873897" y1="44.976700" x2="160.873897" y2="51.126700" style="stroke:rgb(255,0,0);stroke-width:0.10" /> \n  <polygon points="160.873897,51.126700 160.373897,53.126700 160.873897,53.626700 161.373897,53.126700" style="fill:rgb(255,0,0);stroke:rgb(255,0,0);stroke-width:0" /><polygon points="160.873897,44.976700 161.373897,42.976700 160.873897,42.476700 160.373897,42.976700" style="fill:rgb(255,0,0);stroke:rgb(255,0,0);stroke-width:0" /> \n  <text x="158.873897" y="48.051700" font-family="inherit" font-size="3.6" fill="rgb(0,0,0)" text-anchor="middle" transform="rotate(-90.000000 158.873897,48.051700)" >4.1</text> </g>
  Visible = true
  X = 0
  Y = 0
  arrowL1 = 2
  arrowL2 = 0.5
  arrowW = 1
  arrow_scheme = 0
  autoPlaceOffset = 2
  autoPlaceText = true
  click1_x = 160.874
  click1_y = 50.7582
  click2_x = 160.874
  click2_y = 50.7582
  comma_decimal_place = false
  dimension_line_overshoot = 1
  gap_datum_points = 0
  halfDimension_linear = false
  lineColor = rgb(255,0,0)
  strokeWidth = 0.1
  textFormat_linear = %(value)3.3f
  textRenderer_color = rgb(0,0,0)
  textRenderer_family = inherit
  textRenderer_size = 3.6
  unit_custom_scale = 1
  unit_scheme = 0
FEATURE [Drawing::FeatureViewPython] dim014  # drawing view (typed FeaturePython)
  Rotation = 0
  ViewResult = <g> \n  <line x1="163.500000" y1="42.051700" x2="172.294678" y2="42.051700" style="stroke:rgb(255,0,0);stroke-width:0.10" />\n<line x1="163.500000" y1="54.051700" x2="172.294678" y2="54.051700" style="stroke:rgb(255,0,0);stroke-width:0.10" />\n<line x1="171.294678" y1="42.051700" x2="171.294678" y2="54.051700" style="stroke:rgb(255,0,0);stroke-width:0.10" /> \n  <polygon points="171.294678,54.051700 171.794678,52.051700 171.294678,51.551700 170.794678,52.051700" style="fill:rgb(255,0,0);stroke:rgb(255,0,0);stroke-width:0" /><polygon points="171.294678,42.051700 170.794678,44.051700 171.294678,44.551700 171.794678,44.051700" style="fill:rgb(255,0,0);stroke:rgb(255,0,0);stroke-width:0" /> \n  <text x="169.294678" y="48.051700" font-family="inherit" font-size="3.6" fill="rgb(0,0,0)" text-anchor="middle" transform="rotate(-90.000000 169.294678,48.051700)" >8</text> </g>
  Visible = true
  X = 0
  Y = 0
  arrowL1 = 2
  arrowL2 = 0.5
  arrowW = 1
  arrow_scheme = 0
  autoPlaceOffset = 2
  autoPlaceText = true
  click1_x = 171.295
  click1_y = 53.9747
  click2_x = 171.295
  click2_y = 53.9747
  comma_decimal_place = false
  dimension_line_overshoot = 1
  gap_datum_points = 0
  halfDimension_linear = false
  lineColor = rgb(255,0,0)
  strokeWidth = 0.1
  textFormat_linear = %(value)3.3f
  textRenderer_color = rgb(0,0,0)
  textRenderer_family = inherit
  textRenderer_size = 3.6
  unit_custom_scale = 1
  unit_scheme = 0
FEATURE [Drawing::FeatureViewPython] dim013  # drawing view (typed FeaturePython)
  Rotation = 0
  ViewResult = <g> \n  <line x1="163.500000" y1="32.301700" x2="181.312670" y2="32.301700" style="stroke:rgb(255,0,0);stroke-width:0.10" />\n<line x1="163.500000" y1="63.801700" x2="181.312670" y2="63.801700" style="stroke:rgb(255,0,0);stroke-width:0.10" />\n<line x1="180.312670" y1="32.301700" x2="180.312670" y2="63.801700" style="stroke:rgb(255,0,0);stroke-width:0.10" /> \n  <polygon points="180.312670,63.801700 180.812670,61.801700 180.312670,61.301700 179.812670,61.801700" style="fill:rgb(255,0,0);stroke:rgb(255,0,0);stroke-width:0" /><polygon points="180.312670,32.301700 179.812670,34.301700 180.312670,34.801700 180.812670,34.301700" style="fill:rgb(255,0,0);stroke:rgb(255,0,0);stroke-width:0" /> \n  <text x="178.312670" y="48.051700" font-family="inherit" font-size="3.6" fill="rgb(0,0,0)" text-anchor="middle" transform="rotate(-90.000000 178.312670,48.051700)" >21</text> </g>
  Visible = true
  X = 0
  Y = 0
  arrowL1 = 2
  arrowL2 = 0.5
  arrowW = 1
  arrow_scheme = 0
  autoPlaceOffset = 2
  autoPlaceText = true
  click1_x = 180.313
  click1_y = 64.2546
  click2_x = 180.313
  click2_y = 64.2546
  comma_decimal_place = false
  dimension_line_overshoot = 1
  gap_datum_points = 0
  halfDimension_linear = false
  lineColor = rgb(255,0,0)
  strokeWidth = 0.1
  textFormat_linear = %(value)3.3f
  textRenderer_color = rgb(0,0,0)
  textRenderer_family = inherit
  textRenderer_size = 3.6
  unit_custom_scale = 1
  unit_scheme = 0
FEATURE [Drawing::FeatureViewPython] dim015  # drawing view (typed FeaturePython)
  Rotation = 0
  ViewResult = <g> \n  <line x1="213.000000" y1="29.301700" x2="229.377580" y2="29.301700" style="stroke:rgb(255,0,0);stroke-width:0.10" />\n<line x1="213.000000" y1="66.801700" x2="229.377580" y2="66.801700" style="stroke:rgb(255,0,0);stroke-width:0.10" />\n<line x1="228.377580" y1="29.301700" x2="228.377580" y2="66.801700" style="stroke:rgb(255,0,0);stroke-width:0.10" /> \n  <polygon points="228.377580,66.801700 228.877580,64.801700 228.377580,64.301700 227.877580,64.801700" style="fill:rgb(255,0,0);stroke:rgb(255,0,0);stroke-width:0" /><polygon points="228.377580,29.301700 227.877580,31.301700 228.377580,31.801700 228.877580,31.301700" style="fill:rgb(255,0,0);stroke:rgb(255,0,0);stroke-width:0" /> \n  <text x="226.377580" y="48.051700" font-family="inherit" font-size="3.6" fill="rgb(0,0,0)" text-anchor="middle" transform="rotate(-90.000000 226.377580,48.051700)" >25</text> </g>
  Visible = true
  X = 0
  Y = 0
  arrowL1 = 2
  arrowL2 = 0.5
  arrowW = 1
  arrow_scheme = 0
  autoPlaceOffset = 2
  autoPlaceText = true
  click1_x = 228.378
  click1_y = 67.6674
  click2_x = 228.378
  click2_y = 67.6674
  comma_decimal_place = false
  dimension_line_overshoot = 1
  gap_datum_points = 0
  halfDimension_linear = false
  lineColor = rgb(255,0,0)
  strokeWidth = 0.1
  textFormat_linear = %(value)3.3f
  textRenderer_color = rgb(0,0,0)
  textRenderer_family = inherit
  textRenderer_size = 3.6
  unit_custom_scale = 1
  unit_scheme = 0
FEATURE [Drawing::FeatureViewPython] dim016  # drawing view (typed FeaturePython)
  Rotation = 0
  ViewResult = <g> \n  <line x1="213.000000" y1="91.285000" x2="213.000000" y2="82.255193" style="stroke:rgb(255,0,0);stroke-width:0.10" />\n<line x1="191.250000" y1="91.821550" x2="191.250000" y2="82.255193" style="stroke:rgb(255,0,0);stroke-width:0.10" />\n<line x1="213.000000" y1="83.255193" x2="191.250000" y2="83.255193" style="stroke:rgb(255,0,0);stroke-width:0.10" /> \n  <polygon points="191.250000,83.255193 193.250000,83.755193 193.750000,83.255193 193.250000,82.755193" style="fill:rgb(255,0,0);stroke:rgb(255,0,0);stroke-width:0" /><polygon points="213.000000,83.255193 211.000000,82.755193 210.500000,83.255193 211.000000,83.755193" style="fill:rgb(255,0,0);stroke:rgb(255,0,0);stroke-width:0" /> \n  <text x="202.125000" y="81.255193" font-family="inherit" font-size="3.6" fill="rgb(0,0,0)" text-anchor="middle" transform="rotate(0.000000 202.125000,81.255193)" >14.5</text> </g>
  Visible = true
  X = 0
  Y = 0
  arrowL1 = 2
  arrowL2 = 0.5
  arrowW = 1
  arrow_scheme = 0
  autoPlaceOffset = 2
  autoPlaceText = true
  click1_x = 192.064
  click1_y = 83.2552
  click2_x = 192.064
  click2_y = 83.2552
  comma_decimal_place = false
  dimension_line_overshoot = 1
  gap_datum_points = 0
  halfDimension_linear = false
  lineColor = rgb(255,0,0)
  strokeWidth = 0.1
  textFormat_linear = %(value)3.3f
  textRenderer_color = rgb(0,0,0)
  textRenderer_family = inherit
  textRenderer_size = 3.6
  unit_custom_scale = 1
  unit_scheme = 0
FEATURE [Drawing::FeatureViewPython] dim017  # drawing view (typed FeaturePython)
  Rotation = 0
  ViewResult = <g> \n  <line x1="213.000000" y1="91.285000" x2="213.000000" y2="88.394589" style="stroke:rgb(255,0,0);stroke-width:0.10" />\n<line x1="204.750000" y1="92.035000" x2="204.750000" y2="88.394589" style="stroke:rgb(255,0,0);stroke-width:0.10" />\n<line x1="213.000000" y1="89.394589" x2="204.750000" y2="89.394589" style="stroke:rgb(255,0,0);stroke-width:0.10" /> \n  <polygon points="204.750000,89.394589 206.750000,89.894589 207.250000,89.394589 206.750000,88.894589" style="fill:rgb(255,0,0);stroke:rgb(255,0,0);stroke-width:0" /><polygon points="213.000000,89.394589 211.000000,88.894589 210.500000,89.394589 211.000000,89.894589" style="fill:rgb(255,0,0);stroke:rgb(255,0,0);stroke-width:0" /> \n  <text x="208.875000" y="87.394589" font-family="inherit" font-size="3.6" fill="rgb(0,0,0)" text-anchor="middle" transform="rotate(0.000000 208.875000,87.394589)" >5.5</text> </g>
  Visible = true
  X = 0
  Y = 0
  arrowL1 = 2
  arrowL2 = 0.5
  arrowW = 1
  arrow_scheme = 0
  autoPlaceOffset = 2
  autoPlaceText = true
  click1_x = 204.965
  click1_y = 89.3946
  click2_x = 204.965
  click2_y = 89.3946
  comma_decimal_place = false
  dimension_line_overshoot = 1
  gap_datum_points = 0
  halfDimension_linear = false
  lineColor = rgb(255,0,0)
  strokeWidth = 0.1
  textFormat_linear = %(value)3.3f
  textRenderer_color = rgb(0,0,0)
  textRenderer_family = inherit
  textRenderer_size = 3.6
  unit_custom_scale = 1
  unit_scheme = 0
FEATURE [Drawing::FeatureViewPython] dia007  # drawing view (typed FeaturePython)
  Rotation = 0
  ViewResult = <g>  <circle cx ="191.250648" cy ="110.034580" r="0.250000" stroke="none" fill="rgb(255,0,0)" /> \n<line x1="177.541090" y1="87.239341" x2="193.956650" y2="114.533919" style="stroke:rgb(255,0,0);stroke-width:0.10" />\n<polygon points="188.544646,105.535241 189.146952,107.506846 189.833125,107.677628 190.003907,106.991455" style="fill:rgb(255,0,0);stroke:rgb(255,0,0);stroke-width:0" />\n<polygon points="193.956650,114.533919 193.354344,112.562313 192.668171,112.391532 192.497389,113.077705" style="fill:rgb(255,0,0);stroke:rgb(255,0,0);stroke-width:0" />\n<line x1="177.541090" y1="87.239341" x2="170.631043" y2="87.239341" style="stroke:rgb(255,0,0);stroke-width:0.10" />\n<text x="174.086066" y="85.239341" font-family="inherit" font-size="3.6" fill="rgb(0,0,0)" text-anchor="middle" transform="rotate(0.000000 174.086066,85.239341)" >Ø7</text> </g>
  Visible = true
  X = 0
  Y = 0
  arrowL1 = 2
  arrowL2 = 0.5
  arrowW = 1
  arrow_scheme = 0
  autoPlaceOffset = 2
  autoPlaceText = true
  centerPointDia = 0.5
  click1_x = 177.541
  click1_y = 87.2393
  click2_x = 170.631
  click2_y = 86.5326
  click3_x = 170.631
  click3_y = 86.5326
  comma_decimal_place = false
  lineColor = rgb(255,0,0)
  strokeWidth = 0.1
  textFormat_circular = Ø%(value)3.1f
  textRenderer_color = rgb(0,0,0)
  textRenderer_family = inherit
  textRenderer_size = 3.6
  unit_custom_scale = 1
  unit_scheme = 0
FEATURE [Drawing::FeatureViewPython] dim018  # drawing view (typed FeaturePython)
  Rotation = 0
  ViewResult = <g> \n  <line x1="163.500000" y1="125.785000" x2="163.500000" y2="139.853569" style="stroke:rgb(255,0,0);stroke-width:0.10" />\n<line x1="210.000000" y1="116.035000" x2="210.000000" y2="139.853569" style="stroke:rgb(255,0,0);stroke-width:0.10" />\n<line x1="163.500000" y1="138.853569" x2="210.000000" y2="138.853569" style="stroke:rgb(255,0,0);stroke-width:0.10" /> \n  <polygon points="210.000000,138.853569 208.000000,138.353569 207.500000,138.853569 208.000000,139.353569" style="fill:rgb(255,0,0);stroke:rgb(255,0,0);stroke-width:0" /><polygon points="163.500000,138.853569 165.500000,139.353569 166.000000,138.853569 165.500000,138.353569" style="fill:rgb(255,0,0);stroke:rgb(255,0,0);stroke-width:0" /> \n  <text x="186.750000" y="136.853569" font-family="inherit" font-size="3.6" fill="rgb(0,0,0)" text-anchor="middle" transform="rotate(0.000000 186.750000,136.853569)" >31</text> </g>
  Visible = true
  X = 0
  Y = 0
  arrowL1 = 2
  arrowL2 = 0.5
  arrowW = 1
  arrow_scheme = 0
  autoPlaceOffset = 2
  autoPlaceText = true
  click1_x = 202.149
  click1_y = 138.854
  click2_x = 202.149
  click2_y = 138.854
  comma_decimal_place = false
  dimension_line_overshoot = 1
  gap_datum_points = 0
  halfDimension_linear = false
  lineColor = rgb(255,0,0)
  strokeWidth = 0.1
  textFormat_linear = %(value)3.3f
  textRenderer_color = rgb(0,0,0)
  textRenderer_family = inherit
  textRenderer_size = 3.6
  unit_custom_scale = 1
  unit_scheme = 0
FEATURE [Drawing::FeatureViewPython] dim019  # drawing view (typed FeaturePython)
  Rotation = 0
  ViewResult = <g> \n  <line x1="163.500000" y1="125.785000" x2="163.500000" y2="148.129421" style="stroke:rgb(255,0,0);stroke-width:0.10" />\n<line x1="213.000000" y1="128.785000" x2="213.000000" y2="148.129421" style="stroke:rgb(255,0,0);stroke-width:0.10" />\n<line x1="163.500000" y1="147.129421" x2="213.000000" y2="147.129421" style="stroke:rgb(255,0,0);stroke-width:0.10" /> \n  <polygon points="213.000000,147.129421 211.000000,146.629421 210.500000,147.129421 211.000000,147.629421" style="fill:rgb(255,0,0);stroke:rgb(255,0,0);stroke-width:0" /><polygon points="163.500000,147.129421 165.500000,147.629421 166.000000,147.129421 165.500000,146.629421" style="fill:rgb(255,0,0);stroke:rgb(255,0,0);stroke-width:0" /> \n  <text x="188.250000" y="145.129421" font-family="inherit" font-size="3.6" fill="rgb(0,0,0)" text-anchor="middle" transform="rotate(0.000000 188.250000,145.129421)" >33</text> </g>
  Visible = true
  X = 0
  Y = 0
  arrowL1 = 2
  arrowL2 = 0.5
  arrowW = 1
  arrow_scheme = 0
  autoPlaceOffset = 2
  autoPlaceText = true
  click1_x = 192.265
  click1_y = 147.129
  click2_x = 192.265
  click2_y = 147.129
  comma_decimal_place = false
  dimension_line_overshoot = 1
  gap_datum_points = 0
  halfDimension_linear = false
  lineColor = rgb(255,0,0)
  strokeWidth = 0.1
  textFormat_linear = %(value)3.3f
  textRenderer_color = rgb(0,0,0)
  textRenderer_family = inherit
  textRenderer_size = 3.6
  unit_custom_scale = 1
  unit_scheme = 0
FEATURE [Drawing::FeatureViewPython] dim021  # drawing view (typed FeaturePython)
  Rotation = 0
  ViewResult = <g> \n  <line x1="104.250000" y1="95.335000" x2="104.250000" y2="82.877429" style="stroke:rgb(255,0,0);stroke-width:0.10" />\n<line x1="106.500000" y1="95.335000" x2="106.500000" y2="82.877429" style="stroke:rgb(255,0,0);stroke-width:0.10" />\n<line x1="104.250000" y1="83.877429" x2="106.500000" y2="83.877429" style="stroke:rgb(255,0,0);stroke-width:0.10" /> \n  <polygon points="106.500000,83.877429 108.500000,84.377429 109.000000,83.877429 108.500000,83.377429" style="fill:rgb(255,0,0);stroke:rgb(255,0,0);stroke-width:0" /><polygon points="104.250000,83.877429 102.250000,83.377429 101.750000,83.877429 102.250000,84.377429" style="fill:rgb(255,0,0);stroke:rgb(255,0,0);stroke-width:0" /> \n  <text x="105.375000" y="81.877429" font-family="inherit" font-size="3.6" fill="rgb(0,0,0)" text-anchor="middle" transform="rotate(0.000000 105.375000,81.877429)" >1.5</text> </g>
  Visible = true
  X = 0
  Y = 0
  arrowL1 = 2
  arrowL2 = 0.5
  arrowW = 1
  arrow_scheme = 0
  autoPlaceOffset = 2
  autoPlaceText = true
  click1_x = 106.112
  click1_y = 83.8774
  click2_x = 106.112
  click2_y = 83.8774
  comma_decimal_place = false
  dimension_line_overshoot = 1
  gap_datum_points = 0
  halfDimension_linear = false
  lineColor = rgb(255,0,0)
  strokeWidth = 0.1
  textFormat_linear = %(value)3.3f
  textRenderer_color = rgb(0,0,0)
  textRenderer_family = inherit
  textRenderer_size = 3.6
  unit_custom_scale = 1
  unit_scheme = 0
FEATURE [Drawing::FeatureViewPython] dim022  # drawing view (typed FeaturePython)
  Rotation = 0
  ViewResult = <g> \n  <line x1="99.000000" y1="95.485000" x2="99.000000" y2="88.592858" style="stroke:rgb(255,0,0);stroke-width:0.10" />\n<line x1="102.000000" y1="95.485000" x2="102.000000" y2="88.592858" style="stroke:rgb(255,0,0);stroke-width:0.10" />\n<line x1="99.000000" y1="89.592858" x2="102.000000" y2="89.592858" style="stroke:rgb(255,0,0);stroke-width:0.10" /> \n  <polygon points="102.000000,89.592858 104.000000,90.092858 104.500000,89.592858 104.000000,89.092858" style="fill:rgb(255,0,0);stroke:rgb(255,0,0);stroke-width:0" /><polygon points="99.000000,89.592858 97.000000,89.092858 96.500000,89.592858 97.000000,90.092858" style="fill:rgb(255,0,0);stroke:rgb(255,0,0);stroke-width:0" /> \n  <text x="100.500000" y="87.592858" font-family="inherit" font-size="3.6" fill="rgb(0,0,0)" text-anchor="middle" transform="rotate(0.000000 100.500000,87.592858)" >2</text> </g>
  Visible = true
  X = 0
  Y = 0
  arrowL1 = 2
  arrowL2 = 0.5
  arrowW = 1
  arrow_scheme = 0
  autoPlaceOffset = 2
  autoPlaceText = true
  click1_x = 101.862
  click1_y = 89.5929
  click2_x = 101.862
  click2_y = 89.5929
  comma_decimal_place = false
  dimension_line_overshoot = 1
  gap_datum_points = 0
  halfDimension_linear = false
  lineColor = rgb(255,0,0)
  strokeWidth = 0.1
  textFormat_linear = %(value)3.3f
  textRenderer_color = rgb(0,0,0)
  textRenderer_family = inherit
  textRenderer_size = 3.6
  unit_custom_scale = 1
  unit_scheme = 0
FEATURE [Drawing::FeatureViewPython] dim023  # drawing view (typed FeaturePython)
  Rotation = 0
  ViewResult = <g> \n  <line x1="84.000000" y1="108.910000" x2="78.994675" y2="108.910000" style="stroke:rgb(255,0,0);stroke-width:0.10" />\n<line x1="84.000000" y1="111.160000" x2="78.994675" y2="111.160000" style="stroke:rgb(255,0,0);stroke-width:0.10" />\n<line x1="79.994675" y1="108.910000" x2="79.994675" y2="111.160000" style="stroke:rgb(255,0,0);stroke-width:0.10" /> \n  <polygon points="79.994675,111.160000 79.494675,113.160000 79.994675,113.660000 80.494675,113.160000" style="fill:rgb(255,0,0);stroke:rgb(255,0,0);stroke-width:0" /><polygon points="79.994675,108.910000 80.494675,106.910000 79.994675,106.410000 79.494675,106.910000" style="fill:rgb(255,0,0);stroke:rgb(255,0,0);stroke-width:0" /> \n  <text x="77.994675" y="110.035000" font-family="inherit" font-size="3.6" fill="rgb(0,0,0)" text-anchor="middle" transform="rotate(-90.000000 77.994675,110.035000)" >1.5</text> </g>
  Visible = true
  X = 0
  Y = 0
  arrowL1 = 2
  arrowL2 = 0.5
  arrowW = 1
  arrow_scheme = 0
  autoPlaceOffset = 2
  autoPlaceText = true
  click1_x = 79.9947
  click1_y = 108.518
  click2_x = 79.9947
  click2_y = 108.518
  comma_decimal_place = false
  dimension_line_overshoot = 1
  gap_datum_points = 0
  halfDimension_linear = false
  lineColor = rgb(255,0,0)
  strokeWidth = 0.1
  textFormat_linear = %(value)3.3f
  textRenderer_color = rgb(0,0,0)
  textRenderer_family = inherit
  textRenderer_size = 3.6
  unit_custom_scale = 1
  unit_scheme = 0
FEATURE [Drawing::FeatureViewPython] dim024  # drawing view (typed FeaturePython)
  Rotation = 0
  ViewResult = <g> \n  <line x1="84.000000" y1="111.160000" x2="84.000000" y2="134.327778" style="stroke:rgb(255,0,0);stroke-width:0.10" />\n<line x1="87.000000" y1="111.160000" x2="87.000000" y2="134.327778" style="stroke:rgb(255,0,0);stroke-width:0.10" />\n<line x1="84.000000" y1="133.327778" x2="87.000000" y2="133.327778" style="stroke:rgb(255,0,0);stroke-width:0.10" /> \n  <polygon points="87.000000,133.327778 89.000000,133.827778 89.500000,133.327778 89.000000,132.827778" style="fill:rgb(255,0,0);stroke:rgb(255,0,0);stroke-width:0" /><polygon points="84.000000,133.327778 82.000000,132.827778 81.500000,133.327778 82.000000,133.827778" style="fill:rgb(255,0,0);stroke:rgb(255,0,0);stroke-width:0" /> \n  <text x="85.500000" y="131.327778" font-family="inherit" font-size="3.6" fill="rgb(0,0,0)" text-anchor="middle" transform="rotate(0.000000 85.500000,131.327778)" >2</text> </g>
  Visible = true
  X = 0
  Y = 0
  arrowL1 = 2
  arrowL2 = 0.5
  arrowW = 1
  arrow_scheme = 0
  autoPlaceOffset = 2
  autoPlaceText = true
  click1_x = 86.362
  click1_y = 133.328
  click2_x = 86.362
  click2_y = 133.328
  comma_decimal_place = false
  dimension_line_overshoot = 1
  gap_datum_points = 0
  halfDimension_linear = false
  lineColor = rgb(255,0,0)
  strokeWidth = 0.1
  textFormat_linear = %(value)3.3f
  textRenderer_color = rgb(0,0,0)
  textRenderer_family = inherit
  textRenderer_size = 3.6
  unit_custom_scale = 1
  unit_scheme = 0
FEATURE [Drawing::FeatureViewPython] dim025  # drawing view (typed FeaturePython)
  Rotation = 0
  ViewResult = <g> \n  <line x1="37.527300" y1="108.910000" x2="29.966452" y2="108.910000" style="stroke:rgb(255,0,0);stroke-width:0.10" />\n<line x1="37.527300" y1="111.160000" x2="29.966452" y2="111.160000" style="stroke:rgb(255,0,0);stroke-width:0.10" />\n<line x1="30.966452" y1="108.910000" x2="30.966452" y2="111.160000" style="stroke:rgb(255,0,0);stroke-width:0.10" /> \n  <polygon points="30.966452,111.160000 30.466452,113.160000 30.966452,113.660000 31.466452,113.160000" style="fill:rgb(255,0,0);stroke:rgb(255,0,0);stroke-width:0" /><polygon points="30.966452,108.910000 31.466452,106.910000 30.966452,106.410000 30.466452,106.910000" style="fill:rgb(255,0,0);stroke:rgb(255,0,0);stroke-width:0" /> \n  <text x="28.966452" y="110.035000" font-family="inherit" font-size="3.6" fill="rgb(0,0,0)" text-anchor="middle" transform="rotate(-90.000000 28.966452,110.035000)" >1.5</text> </g>
  Visible = true
  X = 0
  Y = 0
  arrowL1 = 2
  arrowL2 = 0.5
  arrowW = 1
  arrow_scheme = 0
  autoPlaceOffset = 2
  autoPlaceText = true
  click1_x = 30.9665
  click1_y = 110.877
  click2_x = 30.9665
  click2_y = 110.877
  comma_decimal_place = false
  dimension_line_overshoot = 1
  gap_datum_points = 0
  halfDimension_linear = false
  lineColor = rgb(255,0,0)
  strokeWidth = 0.1
  textFormat_linear = %(value)3.3f
  textRenderer_color = rgb(0,0,0)
  textRenderer_family = inherit
  textRenderer_size = 3.6
  unit_custom_scale = 1
  unit_scheme = 0
FEATURE [Drawing::FeatureViewPython] dim009  # drawing view (typed FeaturePython)
  Rotation = 0
  ViewResult = <g> \n  <line x1="102.000000" y1="126.385000" x2="102.000000" y2="134.040506" style="stroke:rgb(255,0,0);stroke-width:0.10" />\n<line x1="104.250000" y1="126.385000" x2="104.250000" y2="134.040506" style="stroke:rgb(255,0,0);stroke-width:0.10" />\n<line x1="102.000000" y1="133.040506" x2="104.250000" y2="133.040506" style="stroke:rgb(255,0,0);stroke-width:0.10" /> \n  <polygon points="104.250000,133.040506 106.250000,133.540506 106.750000,133.040506 106.250000,132.540506" style="fill:rgb(255,0,0);stroke:rgb(255,0,0);stroke-width:0" /><polygon points="102.000000,133.040506 100.000000,132.540506 99.500000,133.040506 100.000000,133.540506" style="fill:rgb(255,0,0);stroke:rgb(255,0,0);stroke-width:0" /> \n  <text x="103.125000" y="131.040506" font-family="inherit" font-size="3.6" fill="rgb(0,0,0)" text-anchor="middle" transform="rotate(0.000000 103.125000,131.040506)" >1.5</text> </g>
  Visible = true
  X = 0
  Y = 0
  arrowL1 = 2
  arrowL2 = 0.5
  arrowW = 1
  arrow_scheme = 0
  autoPlaceOffset = 2
  autoPlaceText = true
  click1_x = 102.414
  click1_y = 133.041
  click2_x = 102.414
  click2_y = 133.041
  comma_decimal_place = false
  dimension_line_overshoot = 1
  gap_datum_points = 0
  halfDimension_linear = false
  lineColor = rgb(255,0,0)
  strokeWidth = 0.1
  textFormat_linear = %(value)3.3f
  textRenderer_color = rgb(0,0,0)
  textRenderer_family = inherit
  textRenderer_size = 3.6
  unit_custom_scale = 1
  unit_scheme = 0
FEATURE [Drawing::FeatureViewPython] dim010  # drawing view (typed FeaturePython)
  Rotation = 0
  ViewResult = <g> \n  <line x1="106.500000" y1="126.385000" x2="106.500000" y2="141.488814" style="stroke:rgb(255,0,0);stroke-width:0.10" />\n<line x1="108.750000" y1="126.385000" x2="108.750000" y2="141.488814" style="stroke:rgb(255,0,0);stroke-width:0.10" />\n<line x1="106.500000" y1="140.488814" x2="108.750000" y2="140.488814" style="stroke:rgb(255,0,0);stroke-width:0.10" /> \n  <polygon points="108.750000,140.488814 110.750000,140.988814 111.250000,140.488814 110.750000,139.988814" style="fill:rgb(255,0,0);stroke:rgb(255,0,0);stroke-width:0" /><polygon points="106.500000,140.488814 104.500000,139.988814 104.000000,140.488814 104.500000,140.988814" style="fill:rgb(255,0,0);stroke:rgb(255,0,0);stroke-width:0" /> \n  <text x="107.625000" y="138.488814" font-family="inherit" font-size="3.6" fill="rgb(0,0,0)" text-anchor="middle" transform="rotate(0.000000 107.625000,138.488814)" >1.5</text> </g>
  Visible = true
  X = 0
  Y = 0
  arrowL1 = 2
  arrowL2 = 0.5
  arrowW = 1
  arrow_scheme = 0
  autoPlaceOffset = 2
  autoPlaceText = true
  click1_x = 107.608
  click1_y = 140.489
  click2_x = 107.608
  click2_y = 140.489
  comma_decimal_place = false
  dimension_line_overshoot = 1
  gap_datum_points = 0
  halfDimension_linear = false
  lineColor = rgb(255,0,0)
  strokeWidth = 0.1
  textFormat_linear = %(value)3.3f
  textRenderer_color = rgb(0,0,0)
  textRenderer_family = inherit
  textRenderer_size = 3.6
  unit_custom_scale = 1
  unit_scheme = 0
FEATURE [Drawing::FeatureViewPython] dim026  # drawing view (typed FeaturePython)
  Rotation = 0
  ViewResult = <g> \n  <line x1="111.000000" y1="95.335000" x2="119.134089" y2="95.335000" style="stroke:rgb(255,0,0);stroke-width:0.10" />\n<line x1="111.000000" y1="124.735000" x2="119.134089" y2="124.735000" style="stroke:rgb(255,0,0);stroke-width:0.10" />\n<line x1="118.134089" y1="95.335000" x2="118.134089" y2="124.735000" style="stroke:rgb(255,0,0);stroke-width:0.10" /> \n  <polygon points="118.134089,124.735000 118.634089,122.735000 118.134089,122.235000 117.634089,122.735000" style="fill:rgb(255,0,0);stroke:rgb(255,0,0);stroke-width:0" /><polygon points="118.134089,95.335000 117.634089,97.335000 118.134089,97.835000 118.634089,97.335000" style="fill:rgb(255,0,0);stroke:rgb(255,0,0);stroke-width:0" /> \n  <text x="116.134089" y="110.035000" font-family="inherit" font-size="3.6" fill="rgb(0,0,0)" text-anchor="middle" transform="rotate(-90.000000 116.134089,110.035000)" >19.6</text> </g>
  Visible = true
  X = 0
  Y = 0
  arrowL1 = 2
  arrowL2 = 0.5
  arrowW = 1
  arrow_scheme = 0
  autoPlaceOffset = 2
  autoPlaceText = true
  click1_x = 118.134
  click1_y = 123.779
  click2_x = 118.134
  click2_y = 123.779
  comma_decimal_place = false
  dimension_line_overshoot = 1
  gap_datum_points = 0
  halfDimension_linear = false
  lineColor = rgb(255,0,0)
  strokeWidth = 0.1
  textFormat_linear = %(value)3.3f
  textRenderer_color = rgb(0,0,0)
  textRenderer_family = inherit
  textRenderer_size = 3.6
  unit_custom_scale = 1
  unit_scheme = 0
FEATURE [Drawing::FeatureViewPython] dim027  # drawing view (typed FeaturePython)
  Rotation = 0
  ViewResult = <g> \n  <line x1="108.750000" y1="93.685000" x2="108.750000" y2="88.589311" style="stroke:rgb(255,0,0);stroke-width:0.10" />\n<line x1="111.000000" y1="91.285000" x2="111.000000" y2="88.589311" style="stroke:rgb(255,0,0);stroke-width:0.10" />\n<line x1="108.750000" y1="89.589311" x2="111.000000" y2="89.589311" style="stroke:rgb(255,0,0);stroke-width:0.10" /> \n  <polygon points="111.000000,89.589311 113.000000,90.089311 113.500000,89.589311 113.000000,89.089311" style="fill:rgb(255,0,0);stroke:rgb(255,0,0);stroke-width:0" /><polygon points="108.750000,89.589311 106.750000,89.089311 106.250000,89.589311 106.750000,90.089311" style="fill:rgb(255,0,0);stroke:rgb(255,0,0);stroke-width:0" /> \n  <text x="109.875000" y="87.589311" font-family="inherit" font-size="3.6" fill="rgb(0,0,0)" text-anchor="middle" transform="rotate(0.000000 109.875000,87.589311)" >1.5</text> </g>
  Visible = true
  X = 0
  Y = 0
  arrowL1 = 2
  arrowL2 = 0.5
  arrowW = 1
  arrow_scheme = 0
  autoPlaceOffset = 2
  autoPlaceText = true
  click1_x = 110.154
  click1_y = 89.5893
  click2_x = 110.154
  click2_y = 89.5893
  comma_decimal_place = false
  dimension_line_overshoot = 1
  gap_datum_points = 0
  halfDimension_linear = false
  lineColor = rgb(255,0,0)
  strokeWidth = 0.1
  textFormat_linear = %(value)3.3f
  textRenderer_color = rgb(0,0,0)
  textRenderer_family = inherit
  textRenderer_size = 3.6
  unit_custom_scale = 1
  unit_scheme = 0
FEATURE [Drawing::FeatureViewPython] dim020  # drawing view (typed FeaturePython)
  Rotation = 0
  ViewResult = <g> \n  <line x1="108.750000" y1="93.685000" x2="126.473625" y2="93.685000" style="stroke:rgb(255,0,0);stroke-width:0.10" />\n<line x1="108.750000" y1="126.385000" x2="126.473625" y2="126.385000" style="stroke:rgb(255,0,0);stroke-width:0.10" />\n<line x1="125.473625" y1="93.685000" x2="125.473625" y2="126.385000" style="stroke:rgb(255,0,0);stroke-width:0.10" /> \n  <polygon points="125.473625,126.385000 125.973625,124.385000 125.473625,123.885000 124.973625,124.385000" style="fill:rgb(255,0,0);stroke:rgb(255,0,0);stroke-width:0" /><polygon points="125.473625,93.685000 124.973625,95.685000 125.473625,96.185000 125.973625,95.685000" style="fill:rgb(255,0,0);stroke:rgb(255,0,0);stroke-width:0" /> \n  <text x="123.473625" y="110.035000" font-family="inherit" font-size="3.6" fill="rgb(0,0,0)" text-anchor="middle" transform="rotate(-90.000000 123.473625,110.035000)" >21.8</text> </g>
  Visible = true
  X = 0
  Y = 0
  arrowL1 = 2
  arrowL2 = 0.5
  arrowW = 1
  arrow_scheme = 0
  autoPlaceOffset = 2
  autoPlaceText = true
  click1_x = 125.474
  click1_y = 124.71
  click2_x = 125.474
  click2_y = 124.71
  comma_decimal_place = false
  dimension_line_overshoot = 1
  gap_datum_points = 0
  halfDimension_linear = false
  lineColor = rgb(255,0,0)
  strokeWidth = 0.1
  textFormat_linear = %(value)3.3f
  textRenderer_color = rgb(0,0,0)
  textRenderer_family = inherit
  textRenderer_size = 3.6
  unit_custom_scale = 1
  unit_scheme = 0
FEATURE [Drawing::FeatureViewPython] dim028  # drawing view (typed FeaturePython)
  Rotation = 0
  ViewResult = <g> \n  <line x1="84.000000" y1="31.740400" x2="75.913583" y2="31.740400" style="stroke:rgb(255,0,0);stroke-width:0.10" />\n<line x1="85.380000" y1="64.363000" x2="75.913583" y2="64.363000" style="stroke:rgb(255,0,0);stroke-width:0.10" />\n<line x1="76.913583" y1="31.740400" x2="76.913583" y2="64.363000" style="stroke:rgb(255,0,0);stroke-width:0.10" /> \n  <polygon points="76.913583,64.363000 77.413583,62.363000 76.913583,61.863000 76.413583,62.363000" style="fill:rgb(255,0,0);stroke:rgb(255,0,0);stroke-width:0" /><polygon points="76.913583,31.740400 76.413583,33.740400 76.913583,34.240400 77.413583,33.740400" style="fill:rgb(255,0,0);stroke:rgb(255,0,0);stroke-width:0" /> \n  <text x="74.913583" y="48.051700" font-family="inherit" font-size="3.6" fill="rgb(0,0,0)" text-anchor="middle" transform="rotate(-90.000000 74.913583,48.051700)" >21.748</text> </g>
  Visible = true
  X = 0
  Y = 0
  arrowL1 = 2
  arrowL2 = 0.5
  arrowW = 1
  arrow_scheme = 0
  autoPlaceOffset = 2
  autoPlaceText = true
  click1_x = 76.9136
  click1_y = 63.6478
  click2_x = 76.9136
  click2_y = 63.6478
  comma_decimal_place = false
  dimension_line_overshoot = 1
  gap_datum_points = 0
  halfDimension_linear = false
  lineColor = rgb(255,0,0)
  strokeWidth = 0.1
  textFormat_linear = %(value)3.3f
  textRenderer_color = rgb(0,0,0)
  textRenderer_family = inherit
  textRenderer_size = 3.6
  unit_custom_scale = 1
  unit_scheme = 0
FEATURE [Drawing::FeatureViewPython] dim029  # drawing view (typed FeaturePython)
  Rotation = 0
  ViewResult = <g> \n  <line x1="85.380000" y1="64.363000" x2="80.457364" y2="64.363000" style="stroke:rgb(255,0,0);stroke-width:0.10" />\n<line x1="84.348000" y1="62.574595" x2="80.457364" y2="62.574595" style="stroke:rgb(255,0,0);stroke-width:0.10" />\n<line x1="81.457364" y1="64.363000" x2="81.457364" y2="62.574595" style="stroke:rgb(255,0,0);stroke-width:0.10" /> \n  <polygon points="81.457364,62.574595 81.957364,60.574595 81.457364,60.074595 80.957364,60.574595" style="fill:rgb(255,0,0);stroke:rgb(255,0,0);stroke-width:0" /><polygon points="81.457364,64.363000 80.957364,66.363000 81.457364,66.863000 81.957364,66.363000" style="fill:rgb(255,0,0);stroke:rgb(255,0,0);stroke-width:0" /> \n  <text x="79.457364" y="63.468797" font-family="inherit" font-size="3.6" fill="rgb(0,0,0)" text-anchor="middle" transform="rotate(-90.000000 79.457364,63.468797)" >1.192</text> </g>
  Visible = true
  X = 0
  Y = 0
  arrowL1 = 2
  arrowL2 = 0.5
  arrowW = 1
  arrow_scheme = 0
  autoPlaceOffset = 2
  autoPlaceText = true
  click1_x = 81.4574
  click1_y = 62.8358
  click2_x = 81.4574
  click2_y = 62.8358
  comma_decimal_place = false
  dimension_line_overshoot = 1
  gap_datum_points = 0
  halfDimension_linear = false
  lineColor = rgb(255,0,0)
  strokeWidth = 0.1
  textFormat_linear = %(value)3.3f
  textRenderer_color = rgb(0,0,0)
  textRenderer_family = inherit
  textRenderer_size = 3.6
  unit_custom_scale = 1
  unit_scheme = 0
FEATURE [Drawing::FeatureViewPython] dim030  # drawing view (typed FeaturePython)
  Rotation = 0
  ViewResult = <g> \n  <line x1="85.570500" y1="64.363000" x2="85.570500" y2="85.254609" style="stroke:rgb(255,0,0);stroke-width:0.10" />\n<line x1="87.844500" y1="64.401700" x2="87.844500" y2="85.254609" style="stroke:rgb(255,0,0);stroke-width:0.10" />\n<line x1="85.570500" y1="84.254609" x2="87.844500" y2="84.254609" style="stroke:rgb(255,0,0);stroke-width:0.10" /> \n  <polygon points="87.844500,84.254609 89.844500,84.754609 90.344500,84.254609 89.844500,83.754609" style="fill:rgb(255,0,0);stroke:rgb(255,0,0);stroke-width:0" /><polygon points="85.570500,84.254609 83.570500,83.754609 83.070500,84.254609 83.570500,84.754609" style="fill:rgb(255,0,0);stroke:rgb(255,0,0);stroke-width:0" /> \n  <text x="86.707500" y="82.254609" font-family="inherit" font-size="3.6" fill="rgb(0,0,0)" text-anchor="middle" transform="rotate(0.000000 86.707500,82.254609)" >1.516</text> </g>
  Visible = true
  X = 0
  Y = 0
  arrowL1 = 2
  arrowL2 = 0.5
  arrowW = 1
  arrow_scheme = 0
  autoPlaceOffset = 2
  autoPlaceText = true
  click1_x = 86.8956
  click1_y = 84.2546
  click2_x = 86.8956
  click2_y = 84.2546
  comma_decimal_place = false
  dimension_line_overshoot = 1
  gap_datum_points = 0
  halfDimension_linear = false
  lineColor = rgb(255,0,0)
  strokeWidth = 0.1
  textFormat_linear = %(value)3.3f
  textRenderer_color = rgb(0,0,0)
  textRenderer_family = inherit
  textRenderer_size = 3.6
  unit_custom_scale = 1
  unit_scheme = 0
FEATURE [Drawing::FeaturePage] Page
  EditableTexts = Dr. Zoidberg | 07.11.2019 | x1.5 | -- | ERG-T-04 | Integral Sensor Holder | 01 | 01
  Group = -> [Ortho,Ortho001,Ortho002,Ortho003,dia001,dia002,dia003,dia004,dia005,dia006,dim001,dim002,dim003,dim004,dim005,dim006,dim007,dim008,dim011,dim012,dim014,dim013,dim015,dim016,dim017,dia007,dim018,dim019,dim021,dim022,dim023,dim024,dim025,dim009,dim010,dim026,dim027,dim020,dim028,dim029,dim030]
  Template = <path>
note: 1 file-system path scrubbed to <path> (originals preserved in the JSON sidecar)
